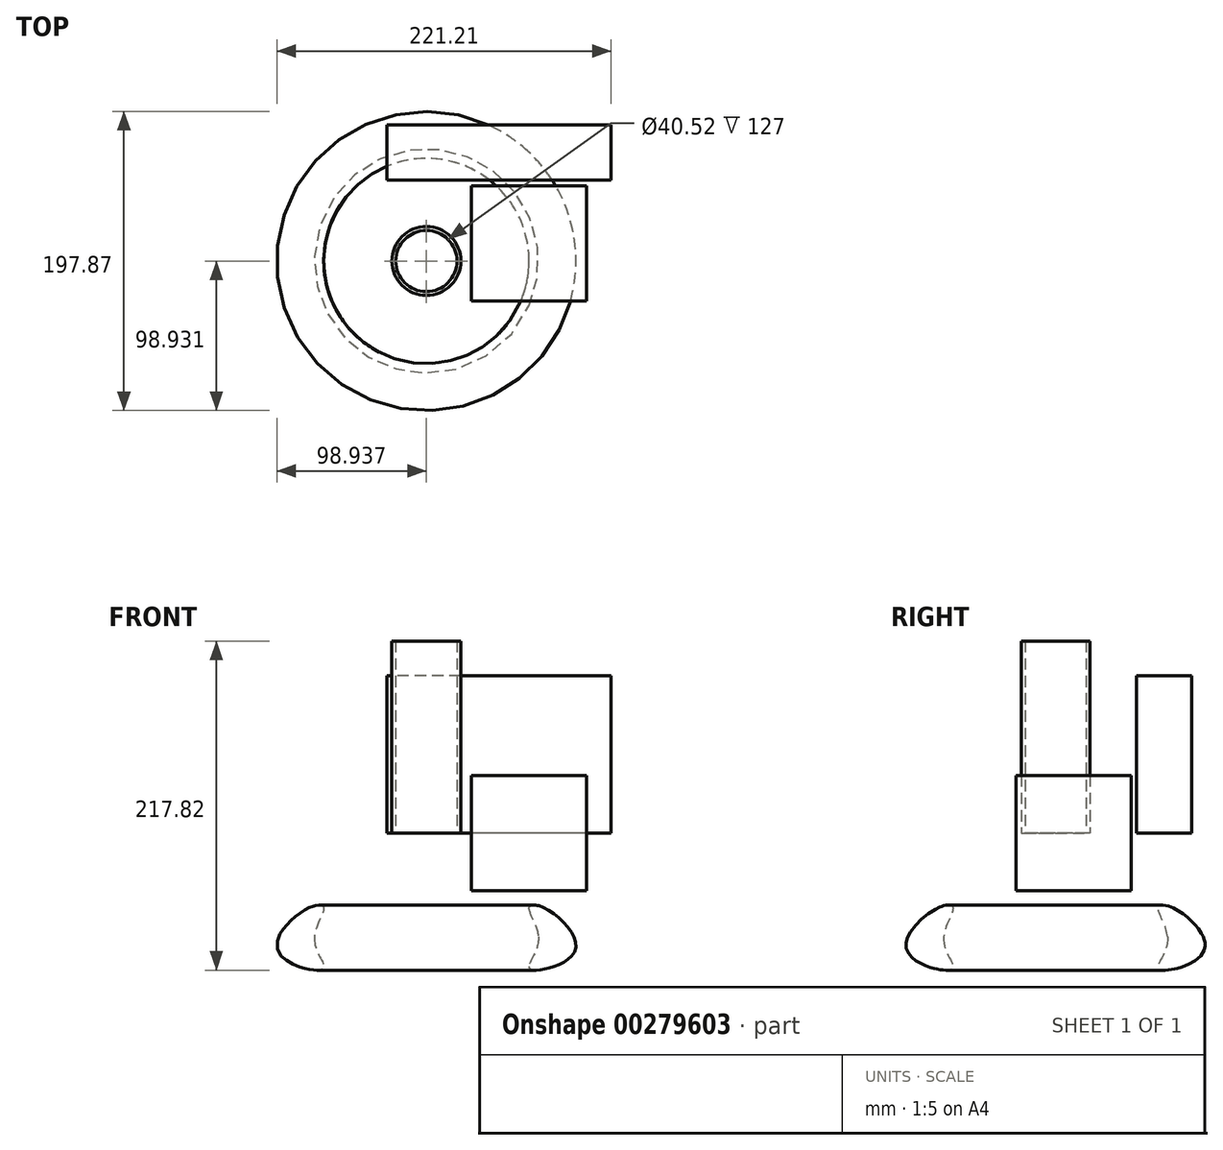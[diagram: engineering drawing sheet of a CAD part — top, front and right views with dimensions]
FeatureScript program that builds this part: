
annotation { "Feature Type Name" : "Feature", "Feature Type Description" : "" }
export const myFeature = defineFeature(function(context is Context, id is Id, definition is map)
    precondition{}
    {
        {
            var Q0;
            Q0=qCreatedBy(makeId("Front.planeOp"),FACE);
            var sketch = newSketch(context, id + "F0", { "sketchPlane" : qUnion([Q0])});
            skLineSegment(sketch, "E0.bottom", {"start": v(38.1, 38.1) * mm, "end": v(-38.1, 38.1) * mm});
            skLineSegment(sketch, "E0.top", {"start": v(38.1, -38.1) * mm, "end": v(-38.1, -38.1) * mm});
            skLineSegment(sketch, "E0.left", {"start": v(38.1, 38.1) * mm, "end": v(38.1, -38.1) * mm});
            skLineSegment(sketch, "E0.right", {"start": v(-38.1, 38.1) * mm, "end": v(-38.1, -38.1) * mm});
            skPoint(sketch, "E0.middle", {"position": v(0, 0) * mm});
            skSolve(sketch);
        }
        {
            var Q0;
            Q0 = qSketchRegion(id + "F0", true);
            extrude(context, id + "F1", {"entities" : qUnion([Q0]), "depth" : 76.2 * mm});
        }
        {
            var Q0;
            Q0=qCreatedBy(makeId("Top.planeOp"),FACE);
            var sketch = newSketch(context, id + "F2", { "sketchPlane" : qUnion([Q0])});
            skLineSegment(sketch, "E1.bottom", {"start": v(54.36, 3.53) * mm, "end": v(-93.9, 3.53) * mm});
            skLineSegment(sketch, "E1.top", {"start": v(54.36, 40.24) * mm, "end": v(-93.9, 40.24) * mm});
            skLineSegment(sketch, "E1.left", {"start": v(54.36, 3.53) * mm, "end": v(54.36, 40.24) * mm});
            skLineSegment(sketch, "E1.right", {"start": v(-93.9, 3.53) * mm, "end": v(-93.9, 40.24) * mm});
            skPoint(sketch, "E1.middle", {"position": v(-19.77, 21.89) * mm});
            skSolve(sketch);
        }
        {
            var Q0;
            Q0 = qSketchRegion(id + "F2", true);
            extrude(context, id + "F3", {"entities" : qUnion([Q0]), "depth" : 104.14 * mm});
        }
        {
            var Q0;
            Q0=qCreatedBy(makeId("Top.planeOp"),FACE);
            var sketch = newSketch(context, id + "F4", { "sketchPlane" : qUnion([Q0])});
            skCircle(sketch, "E2", {"center": v(-67.91, -49.89) * mm, "radius": 22.8 * mm});
            skSolve(sketch);
        }
        {
            var Q0;
            Q0=makeQuery(id+"F4.imprint","IMPRINT",FACE,{"disambiguationData":[TD([[makeQuery(id+"F4.imprint","IMPRINT",EDGE,{"derivedFrom":sQuery(id+"F4.wireOp",EDGE,"E2")}),1.0]])]});
            extrude(context, id + "F5", {"entities" : qUnion([Q0]), "depth" : 127 * mm});
        }
        {
            var Q0;
            Q0=makeQuery(id+"F5.opExtrude","CAP_FACE",FACE,{"disambiguationData":[OSD([sQuery(id+"F4.wireOp",EDGE,"E2")])],"isStart":false});
            shell(context, id + "F6", {"entities" : qUnion([Q0]), "thickness" : 2.54 * mm});
        }
        {
            var Q0;
            Q0=makeQuery(id+"F5.opExtrude","CAP_FACE",FACE,{"disambiguationData":[OSD([sQuery(id+"F4.wireOp",EDGE,"E2")])],"isStart":true});
            var Q1;
            {var subQ0=sQuery(id+"F4.wireOp",EDGE,"E2");Q1=makeQuery(id+"F6.opShell","OFFSET_FACE",FACE,{"disambiguationData":[OSD([subQ0]),TDD([makeQuery(id+"F5.opExtrude","CAP_FACE",FACE,{"disambiguationData":[OSD([subQ0])],"isStart":true})])]});}
            shell(context, id + "F7", {"entities" : qUnion([Q0, Q1]), "thickness" : 2.54 * mm});
        }
        {
            var Q0;
            Q0=qCreatedBy(makeId("Right.planeOp"),FACE);
            var sketch = newSketch(context, id + "F8", { "sketchPlane" : qUnion([Q0])});
            skLineSegment(sketch, "E3", {"start": v(11.07, -48.04) * mm, "end": v(-78.96, -48.04) * mm, "construction": true});
            skFitSpline(sketch, "E4", {"points": [v(-79.46, -68.85) * mm, v(-40.09, -89.92) * mm, v(21.85, -76.13) * mm, v(-21.03, -48.04) * mm, v(-79.46, -68.85) * mm]});
            skSolve(sketch);
        }
        {
            var Q0;
            Q0=makeQuery(id+"F8.imprint","IMPRINT",FACE,{"disambiguationData":[TD([[makeQuery(id+"F8.imprint","IMPRINT",EDGE,{"derivedFrom":sQuery(id+"F8.wireOp",EDGE,"E4")}),1.0]])]});
            var Q1;
            Q1=makeQuery(id+"F5.opExtrude","SWEPT_FACE",FACE,{"disambiguationData":[OSD([sQuery(id+"F4.wireOp",EDGE,"E2")])]});
            revolve(context, id + "F9", {"entities" : qUnion([Q0]), "axis" : qUnion([Q1]), "revolveType" : RevolveType.FULL});
        }
    });
